# Revit family: Storage-Mounted-Teknion-JNMDO-Desktop_Cabinet_Open-R2016
name_source: partatom
category: Furniture
revit_build: Autodesk Revit Architecture 2016 (Build: 20150220_1215(x64)
units: mm (PartAtom-declared; Revit-internal decimal feet)

## family parameters
Always vertical = Yes
Cut with Voids When Loaded = No
OmniClass Number = 23.40.20.00
OmniClass Title = General Furniture and Specialties
Room Calculation Point = No
Shared = Yes
Work Plane-Based = No

## types (4) — shared parameters
Assembly Code = E2020200
Case Finish = Laminate - Teknion - 2T -Crisp Grey
Manufacturer = Teknion
Manufacturer Fax = 416.661.4586
Part Number = JNMDO
Product Documentation Link = http://www.teknion.com
Product Line = Cityline
Product Page URL = http://www.teknion.com
Series = Cityline
Sustainability Data = http://www.teknion.com
URL = www.teknion.com
Unit Weight URL = http://www.teknion.com
Warranty = http://www.teknion.com

## per-type parameters (varying)
| type | Center Divider Vertical Offset | Central Divider Offset | Description | Divider Back Offset | Divider Back Vertical Offset | Divider Front Offset | Facia Thickness | Felt & Fabric | Glass | Model | Solid | not(Solid) |
| Felt Tackboard Facia | 14.36 " | 7.819 " | Desktop Cabinet - Open - Felt Tackboard Facia | 0.811 " | 13.659 " | 0.811 " | 0.551 " | Yes | No | JNMDOE___ | No | Yes |
| Fabric Tackboard Facia | 14.36 " | 7.819 " | Desktop Cabinet - Open - Fabric Tackboard Facia | 0.811 " | 13.659 " | 0.811 " | 0.551 " | Yes | No | JNMDOF___ | No | Yes |
| Magnetic Glass Fascia | 14.36 " | 7.819 " | Desktop Cabinet - Open - Magnetic Glass Facia | 0.811 " | 13.659 " | 0.811 " | 0.138 " | No | Yes | JNMDOM___ | No | Yes |
| Solid Fascia | 0.701 " | 15.638 " | Desktop Cabinet - Open - Solid Facia | 0.701 " | 14.36 " | 0 " | 0.551 " | No | No | JNMDOS___ | Yes | No |

## geometry (parser evidence)
native form markers: Sweep x2
no freeform markers — native parametric forms only
